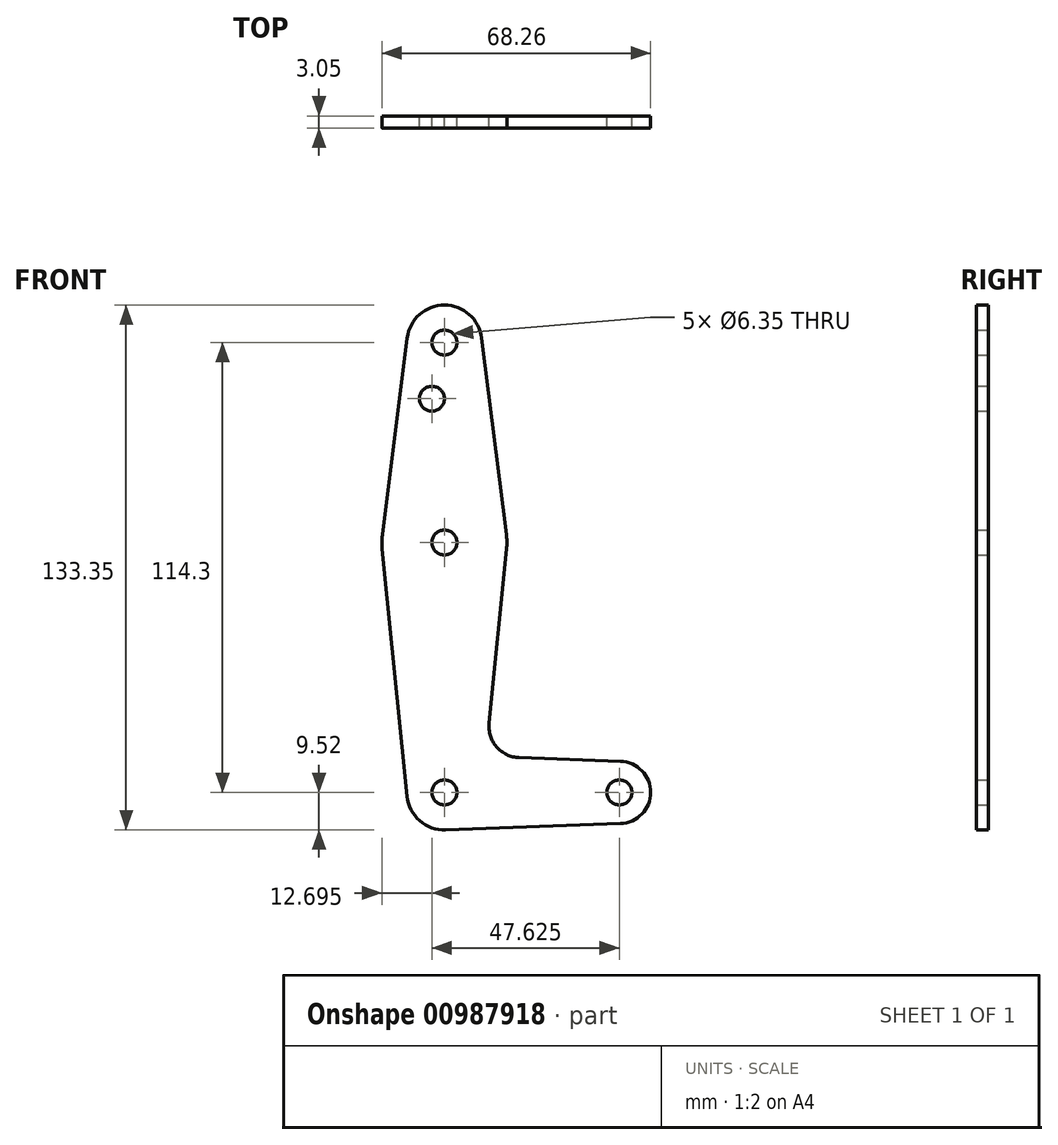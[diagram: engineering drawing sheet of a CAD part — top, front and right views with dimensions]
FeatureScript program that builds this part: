
annotation { "Feature Type Name" : "Feature", "Feature Type Description" : "" }
export const myFeature = defineFeature(function(context is Context, id is Id, definition is map)
    precondition{}
    {
        {
            var Q0;
            Q0=qCreatedBy(makeId("Front.planeOp"),FACE);
            var sketch = newSketch(context, id + "F0", { "sketchPlane" : qUnion([Q0])});
            skLineSegment(sketch, "E0", {"start": v(0, 0) * mm, "end": v(0, 63.5) * mm, "construction": true});
            skLineSegment(sketch, "E1", {"start": v(0, 63.5) * mm, "end": v(0, 114.3) * mm, "construction": true});
            skLineSegment(sketch, "E2", {"start": v(0, 0) * mm, "end": v(44.45, 0) * mm, "construction": true});
            skCircle(sketch, "E3", {"center": v(0, 114.3) * mm, "radius": 9.53 * mm});
            skCircle(sketch, "E4", {"center": v(0, 63.5) * mm, "radius": 15.88 * mm});
            skLineSegment(sketch, "E5", {"start": v(9.45, 115.5) * mm, "end": v(15.75, 65.48) * mm});
            skLineSegment(sketch, "E6", {"start": v(-9.45, 115.5) * mm, "end": v(-15.75, 65.48) * mm});
            skCircle(sketch, "E7", {"center": v(44.45, 0) * mm, "radius": 7.94 * mm});
            skCircle(sketch, "E8", {"center": v(0, 0) * mm, "radius": 9.53 * mm});
            skLineSegment(sketch, "E9", {"start": v(-15.8, 61.91) * mm, "end": v(-9.48, -0.95) * mm});
            skLineSegment(sketch, "E10", {"start": v(15.8, 61.91) * mm, "end": v(11.34, 17.6) * mm});
            skLineSegment(sketch, "E11", {"start": v(44.73, 7.93) * mm, "end": v(18.97, 8.85) * mm});
            skLineSegment(sketch, "E12", {"start": v(44.73, -7.93) * mm, "end": v(0.34, -9.52) * mm});
            skCircle(sketch, "E13", {"center": v(0, 114.3) * mm, "radius": 3.18 * mm});
            skCircle(sketch, "E14", {"center": v(-3.18, 100.03) * mm, "radius": 3.18 * mm});
            skCircle(sketch, "E15", {"center": v(0, 63.5) * mm, "radius": 3.18 * mm});
            skCircle(sketch, "E16", {"center": v(0, 0) * mm, "radius": 3.18 * mm});
            skCircle(sketch, "E17", {"center": v(44.45, 0) * mm, "radius": 3.18 * mm});
            skArc(sketch, "E18.filletArc", {"start": v(11.34, 17.6) * mm, "mid": v(13.26, 11.57) * mm, "end": v(18.97, 8.85) * mm});
            skSolve(sketch);
        }
        {
            var Q0;
            Q0 = qSketchRegion(id + "F0", true);
            extrude(context, id + "F1", {"entities" : qUnion([Q0]), "depth" : 3.05 * mm, "offsetDistance" : 25.4 * mm});
        }
    });
